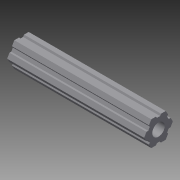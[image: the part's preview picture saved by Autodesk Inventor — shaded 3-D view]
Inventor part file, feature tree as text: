
AUTODESK INVENTOR PART (.ipt)
format: ipt  version: 2015 SP1 (Build 190203100, 203)  size: 138,240 bytes
history: native  units: in
note: dims shown in document units (in); Inventor stores cm internally (conversion verified against a paired STEP export)
features: extrude x1, sketch x1
ambient origin geometry x8: Origin, YZ Plane, XZ Plane, XY Plane, X Axis, Y Axis, Z Axis, Center Point
bodies: Solid1 (feature_tree)
feature tree (2):
  extrude  "Extrusion1"  Depth=0.5in
  sketch  "Sketch1"  dims[d0=0.5in d1=0.5in d2=0.5in d3=120.0deg d4=120.0deg d5=0.25in d6=0.25in d7=0.25in d11=0.0312in d12=0.0938in d13=0.0938in d14=0.0938in d15=0.0938in d16=0.0938in d17=0.0938in d18=0.0938in d19=0.0938in d20=0.0938in d21=0.0938in d22=0.0938in d23=0.0938in d24=150.0deg d25=150.0deg d26=150.0deg d27=90.0deg d28=90.0deg d29=30.0deg d30=30.0deg d31=30.0deg d32=30.0deg d33=90.0deg d34=90.0deg d35=150.0deg d36=0.25in d37=2.75in d38=0.0in]
